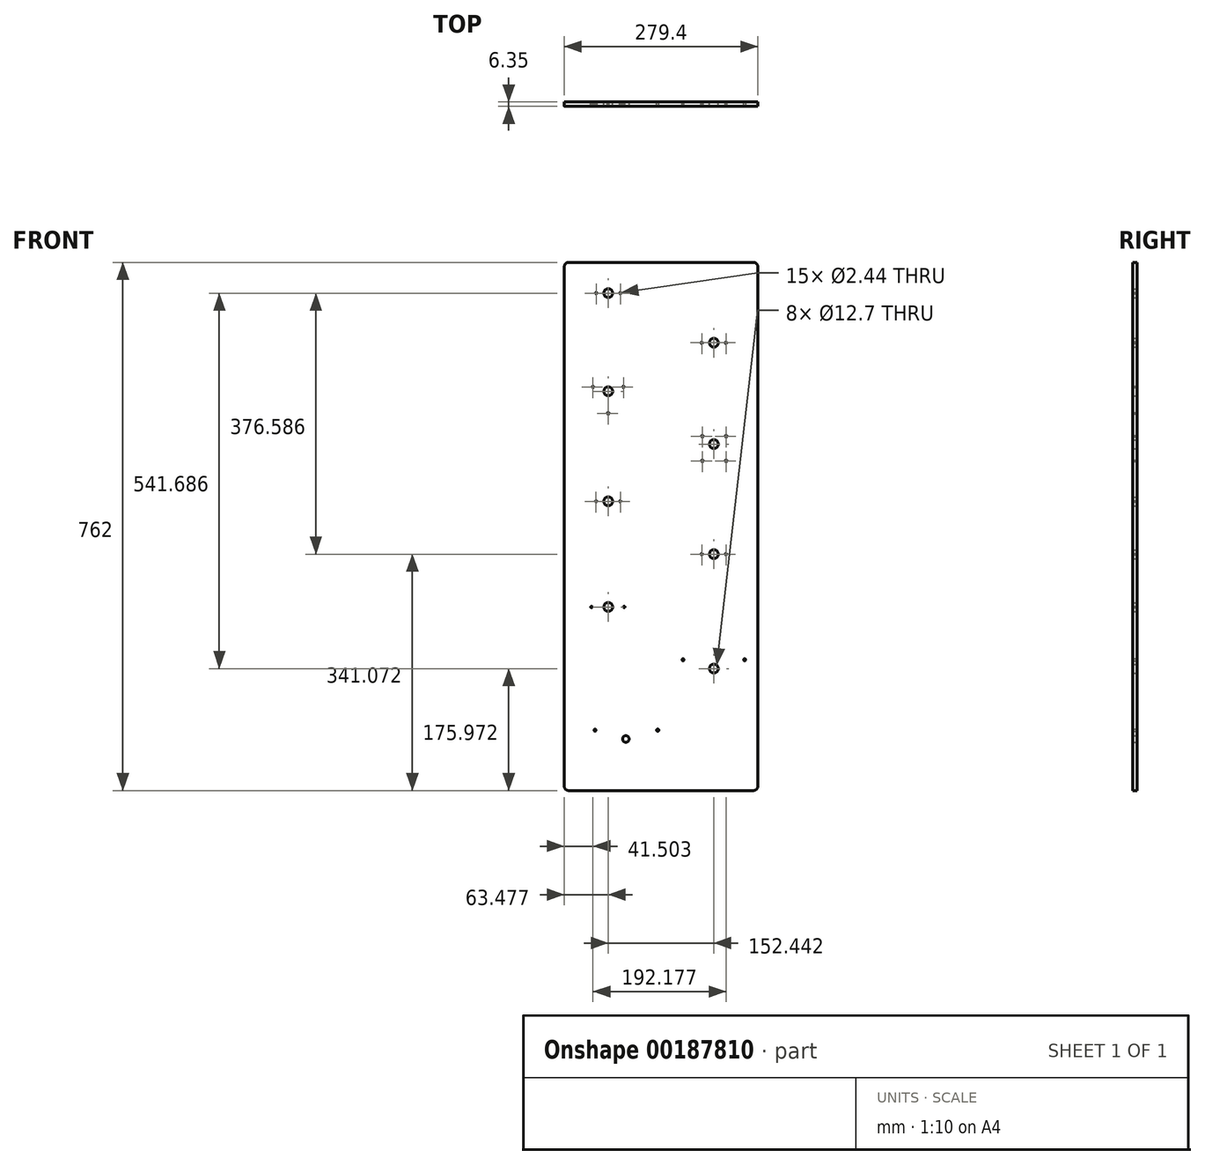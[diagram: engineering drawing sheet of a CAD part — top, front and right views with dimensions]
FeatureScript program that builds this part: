
annotation { "Feature Type Name" : "Feature", "Feature Type Description" : "" }
export const myFeature = defineFeature(function(context is Context, id is Id, definition is map)
    precondition{}
    {
        {
            var Q0;
            Q0=qCreatedBy(makeId("Front.planeOp"),FACE);
            var sketch = newSketch(context, id + "F0", { "sketchPlane" : qUnion([Q0])});
            skLineSegment(sketch, "E0.bottom", {"start": v(133.35, -381) * mm, "end": v(-133.35, -381) * mm});
            skLineSegment(sketch, "E0.top", {"start": v(133.35, 381) * mm, "end": v(-133.35, 381) * mm});
            skLineSegment(sketch, "E0.left", {"start": v(139.7, -374.65) * mm, "end": v(139.7, 374.65) * mm});
            skLineSegment(sketch, "E0.right", {"start": v(-139.7, -374.65) * mm, "end": v(-139.7, 374.65) * mm});
            skPoint(sketch, "E0.middle", {"position": v(0, 0) * mm});
            skLineSegment(sketch, "E1", {"start": v(-123.46, -293.93) * mm, "end": v(223.85, -293.93) * mm, "construction": true});
            skLineSegment(sketch, "E2", {"start": v(-160.35, -192.33) * mm, "end": v(223.85, -192.33) * mm, "construction": true});
            skLineSegment(sketch, "E3", {"start": v(-128.6, -116.13) * mm, "end": v(223.85, -116.13) * mm, "construction": true});
            skLineSegment(sketch, "E4", {"start": v(-145.33, -39.93) * mm, "end": v(223.85, -39.93) * mm, "construction": true});
            skLineSegment(sketch, "E5", {"start": v(-128.04, 36.27) * mm, "end": v(196.11, 36.27) * mm, "construction": true});
            skLineSegment(sketch, "E6", {"start": v(-133.75, 112.47) * mm, "end": v(194.26, 112.47) * mm, "construction": true});
            skLineSegment(sketch, "E7", {"start": v(-140.9, 188.67) * mm, "end": v(206.4, 188.67) * mm, "construction": true});
            skLineSegment(sketch, "E8", {"start": v(-145.33, 264.87) * mm, "end": v(223.85, 264.87) * mm, "construction": true});
            skLineSegment(sketch, "E9", {"start": v(-151.76, 341.07) * mm, "end": v(223.85, 341.07) * mm, "construction": true});
            skLineSegment(sketch, "E10", {"start": v(-50.8, 400.05) * mm, "end": v(-50.8, -398.76) * mm, "construction": true});
            skLineSegment(sketch, "E11", {"start": v(76.2, 397.48) * mm, "end": v(76.2, -396.2) * mm, "construction": true});
            skLineSegment(sketch, "E12", {"start": v(0, 423.93) * mm, "end": v(0, -430.77) * mm, "construction": true});
            skPoint(sketch, "E12.startSnap0", {"position": v(0, 381) * mm});
            skCircle(sketch, "E13", {"center": v(-50.8, -293.93) * mm, "radius": 79.38 * mm, "construction": true});
            skCircle(sketch, "E14", {"center": v(76.2, -192.33) * mm, "radius": 53.98 * mm, "construction": true});
            skLineSegment(sketch, "E15", {"start": v(-76.2, 412.75) * mm, "end": v(-76.2, -262.46) * mm, "construction": true});
            skCircle(sketch, "E16", {"center": v(-76.2, 341.07) * mm, "radius": 22.86 * mm, "construction": true});
            skCircle(sketch, "E17", {"center": v(76.2, 264.87) * mm, "radius": 22.86 * mm, "construction": true});
            skCircle(sketch, "E18", {"center": v(-76.2, 188.67) * mm, "radius": 33.02 * mm, "construction": true});
            skCircle(sketch, "E19", {"center": v(-76.2, 36.27) * mm, "radius": 22.86 * mm, "construction": true});
            skCircle(sketch, "E20", {"center": v(76.2, -39.93) * mm, "radius": 22.86 * mm, "construction": true});
            skCircle(sketch, "E21", {"center": v(-76.2, -116.13) * mm, "radius": 33.02 * mm, "construction": true});
            skLineSegment(sketch, "E22.bottom", {"start": v(111.13, 77.55) * mm, "end": v(41.28, 77.55) * mm, "construction": true});
            skLineSegment(sketch, "E22.top", {"start": v(111.13, 147.4) * mm, "end": v(41.28, 147.4) * mm, "construction": true});
            skLineSegment(sketch, "E22.left", {"start": v(111.13, 77.55) * mm, "end": v(111.13, 147.4) * mm, "construction": true});
            skLineSegment(sketch, "E22.right", {"start": v(41.28, 77.55) * mm, "end": v(41.28, 147.4) * mm, "construction": true});
            skPoint(sketch, "E22.middle", {"position": v(76.2, 112.47) * mm});
            skCircle(sketch, "E23", {"center": v(-95.25, -293.93) * mm, "radius": 1.56 * mm});
            skCircle(sketch, "E24", {"center": v(-4.79, -293.93) * mm, "radius": 1.56 * mm});
            skCircle(sketch, "E25", {"center": v(-50.8, -306.63) * mm, "radius": 4.76 * mm});
            skCircle(sketch, "E26", {"center": v(31.75, -192.33) * mm, "radius": 1.56 * mm});
            skCircle(sketch, "E27", {"center": v(120.65, -192.33) * mm, "radius": 1.56 * mm});
            skCircle(sketch, "E28", {"center": v(76.2, -205.03) * mm, "radius": 6.35 * mm});
            skCircle(sketch, "E29", {"center": v(-76.2, -116.13) * mm, "radius": 6.35 * mm});
            skCircle(sketch, "E30", {"center": v(-100.33, -116.13) * mm, "radius": 1.14 * mm});
            skCircle(sketch, "E31", {"center": v(-53.21, -116.13) * mm, "radius": 1.14 * mm});
            skCircle(sketch, "E32", {"center": v(76.2, -39.93) * mm, "radius": 6.35 * mm});
            skCircle(sketch, "E33", {"center": v(58.74, -39.93) * mm, "radius": 1.22 * mm});
            skCircle(sketch, "E34", {"center": v(93.66, -39.93) * mm, "radius": 1.22 * mm});
            skCircle(sketch, "E35", {"center": v(-76.22, 36.3) * mm, "radius": 6.35 * mm});
            skCircle(sketch, "E36", {"center": v(-93.69, 36.3) * mm, "radius": 1.22 * mm});
            skCircle(sketch, "E37", {"center": v(-58.76, 36.3) * mm, "radius": 1.22 * mm});
            skCircle(sketch, "E38", {"center": v(76.22, 265.02) * mm, "radius": 6.35 * mm});
            skCircle(sketch, "E39", {"center": v(58.76, 265.02) * mm, "radius": 1.22 * mm});
            skCircle(sketch, "E40", {"center": v(93.68, 265.02) * mm, "radius": 1.22 * mm});
            skCircle(sketch, "E41", {"center": v(-76.15, 336.66) * mm, "radius": 6.35 * mm});
            skCircle(sketch, "E42", {"center": v(-93.61, 336.66) * mm, "radius": 1.22 * mm});
            skCircle(sketch, "E43", {"center": v(-58.69, 336.66) * mm, "radius": 1.22 * mm});
            skCircle(sketch, "E44", {"center": v(-76.2, 188.67) * mm, "radius": 25.4 * mm, "construction": true});
            skCircle(sketch, "E45", {"center": v(-76.2, 163.27) * mm, "radius": 1.22 * mm});
            skLineSegment(sketch, "E46", {"start": v(-76.2, 188.67) * mm, "end": v(-116.38, 211.87) * mm, "construction": true});
            skLineSegment(sketch, "E47", {"start": v(-76.2, 188.67) * mm, "end": v(-33.94, 213.07) * mm, "construction": true});
            skCircle(sketch, "E48", {"center": v(-98.2, 201.37) * mm, "radius": 1.22 * mm});
            skCircle(sketch, "E49", {"center": v(-54.2, 201.37) * mm, "radius": 1.22 * mm});
            skCircle(sketch, "E50", {"center": v(-76.2, 195.02) * mm, "radius": 6.35 * mm});
            skCircle(sketch, "E51", {"center": v(59.64, 130.25) * mm, "radius": 1.22 * mm});
            skCircle(sketch, "E52", {"center": v(93.98, 130.25) * mm, "radius": 1.22 * mm});
            skPoint(sketch, "E53.visualSharp", {"position": v(-139.7, 381) * mm});
            skArc(sketch, "E53.filletArc", {"start": v(-133.35, 381) * mm, "mid": v(-137.84, 379.14) * mm, "end": v(-139.7, 374.65) * mm});
            skPoint(sketch, "E54.visualSharp", {"position": v(139.7, 381) * mm});
            skArc(sketch, "E54.filletArc", {"start": v(139.7, 374.65) * mm, "mid": v(137.84, 379.14) * mm, "end": v(133.35, 381) * mm});
            skPoint(sketch, "E55.visualSharp", {"position": v(139.7, -381) * mm});
            skArc(sketch, "E55.filletArc", {"start": v(133.35, -381) * mm, "mid": v(137.84, -379.14) * mm, "end": v(139.7, -374.65) * mm});
            skPoint(sketch, "E56.visualSharp", {"position": v(-139.7, -381) * mm});
            skArc(sketch, "E56.filletArc", {"start": v(-139.7, -374.65) * mm, "mid": v(-137.84, -379.14) * mm, "end": v(-133.35, -381) * mm});
            skCircle(sketch, "E57.MirrorC", {"center": v(93.98, 94.7) * mm, "radius": 1.22 * mm});
            skCircle(sketch, "E58.MirrorC", {"center": v(59.64, 94.7) * mm, "radius": 1.22 * mm});
            skCircle(sketch, "E59", {"center": v(76.2, 118.82) * mm, "radius": 6.35 * mm});
            skSolve(sketch);
        }
        {
            var Q0;
            Q0 = qSketchRegion(id + "F0", true);
            extrude(context, id + "F1", {"entities" : qUnion([Q0]), "depth" : 6.35 * mm});
        }
    });
